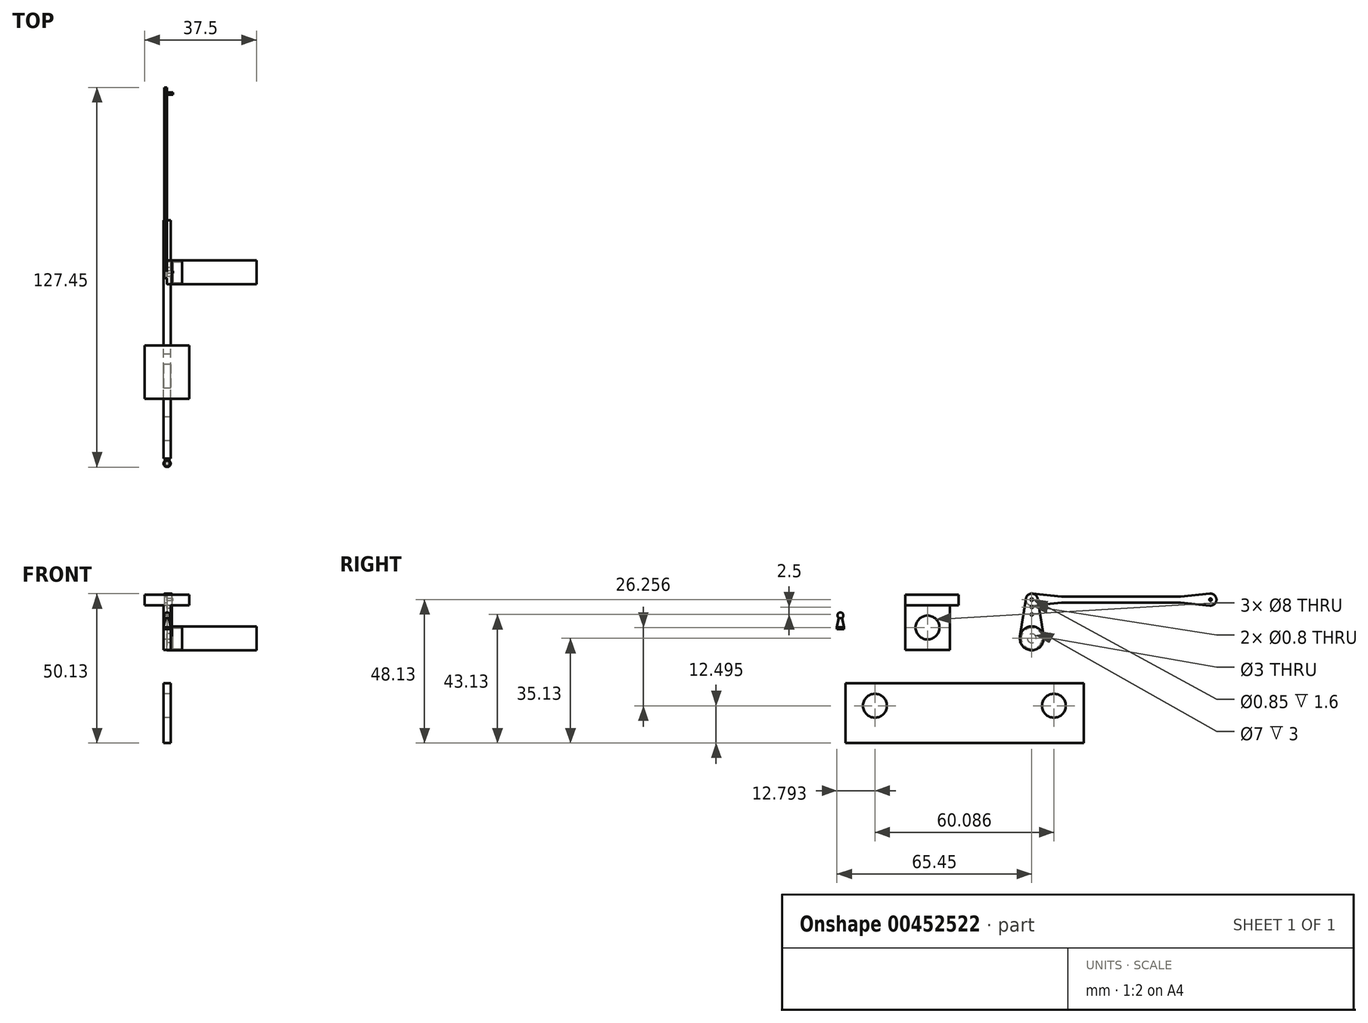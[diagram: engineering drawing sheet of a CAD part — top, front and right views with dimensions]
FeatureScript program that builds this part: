
annotation { "Feature Type Name" : "Feature", "Feature Type Description" : "" }
export const myFeature = defineFeature(function(context is Context, id is Id, definition is map)
    precondition{}
    {
        {
            var Q0;
            Q0=qCreatedBy(makeId("Right.planeOp"),FACE);
            var sketch = newSketch(context, id + "F0", { "sketchPlane" : qUnion([Q0])});
            skCircle(sketch, "E0", {"center": v(0, 0) * mm, "radius": 4 * mm});
            skCircle(sketch, "E1", {"center": v(0, 13) * mm, "radius": 2 * mm});
            skLineSegment(sketch, "E2", {"start": v(-1.98, 13.3) * mm, "end": v(-3.95, 0.62) * mm});
            skLineSegment(sketch, "E3", {"start": v(1.98, 13.3) * mm, "end": v(3.95, 0.62) * mm});
            skLineSegment(sketch, "E4", {"start": v(0, 13) * mm, "end": v(0, 0) * mm, "construction": true});
            skCircle(sketch, "E5", {"center": v(0, 0) * mm, "radius": 1.5 * mm});
            skCircle(sketch, "E6", {"center": v(0, 13) * mm, "radius": 0.42 * mm});
            skCircle(sketch, "E7.0.1.0", {"center": v(0, 10.5) * mm, "radius": 0.4 * mm});
            skLineSegment(sketch, "E7.direction2", {"start": v(0, 13) * mm, "end": v(0, 10.5) * mm, "construction": true});
            skCircle(sketch, "E8.0.1.0", {"center": v(0, 8) * mm, "radius": 0.4 * mm});
            skLineSegment(sketch, "E9", {"start": v(0, 10.5) * mm, "end": v(0, 8) * mm, "construction": true});
            skLineSegment(sketch, "E10", {"start": v(-17.13, 13) * mm, "end": v(24.81, 13) * mm, "construction": true});
            skLineSegment(sketch, "E11", {"start": v(-6.17, 15) * mm, "end": v(18.5, 15) * mm, "construction": true});
            skLineSegment(sketch, "E12", {"start": v(-6.02, 11) * mm, "end": v(18.13, 11) * mm, "construction": true});
            skLineSegment(sketch, "E13", {"start": v(14.47, 16) * mm, "end": v(14.47, 9.33) * mm, "construction": true});
            skCircle(sketch, "E14", {"center": v(9.9, 13) * mm, "radius": 1 * mm});
            skLineSegment(sketch, "E15", {"start": v(0.2, 14.99) * mm, "end": v(10, 14) * mm});
            skLineSegment(sketch, "E16", {"start": v(10, 12) * mm, "end": v(0, 10.99) * mm});
            skCircle(sketch, "E17", {"center": v(0, 13) * mm, "radius": 0.4 * mm});
            skLineSegment(sketch, "E18", {"start": v(10, 14) * mm, "end": v(30, 14) * mm});
            skLineSegment(sketch, "E19.MirrorCS", {"start": v(10, 12) * mm, "end": v(30, 12) * mm});
            skLineSegment(sketch, "E20", {"start": v(30, 14) * mm, "end": v(30, 12) * mm});
            skCircle(sketch, "E21", {"center": v(-35, 3.62) * mm, "radius": 4 * mm});
            skLineSegment(sketch, "E22", {"start": v(-45.57, 1.96) * mm, "end": v(-23.6, 1.96) * mm, "construction": true});
            skLineSegment(sketch, "E23", {"start": v(-35, 12.95) * mm, "end": v(-35, -6.89) * mm, "construction": true});
            skLineSegment(sketch, "E24.bottom", {"start": v(-42.5, 11.12) * mm, "end": v(-27.5, 11.12) * mm});
            skLineSegment(sketch, "E24.top", {"start": v(-42.5, -3.88) * mm, "end": v(-27.5, -3.88) * mm});
            skLineSegment(sketch, "E24.left", {"start": v(-42.5, 11.12) * mm, "end": v(-42.5, -3.88) * mm});
            skLineSegment(sketch, "E24.right", {"start": v(-27.5, 11.12) * mm, "end": v(-27.5, -3.88) * mm});
            skLineSegment(sketch, "E25.bottom", {"start": v(-42.5, 11.12) * mm, "end": v(-24.56, 11.12) * mm});
            skLineSegment(sketch, "E25.top", {"start": v(-42.5, 14.64) * mm, "end": v(-24.56, 14.64) * mm});
            skLineSegment(sketch, "E25.left", {"start": v(-42.5, 11.12) * mm, "end": v(-42.5, 14.64) * mm});
            skLineSegment(sketch, "E25.right", {"start": v(-24.56, 11.12) * mm, "end": v(-24.56, 14.64) * mm});
            skLineSegment(sketch, "E26", {"start": v(10, 14) * mm, "end": v(10, 23.15) * mm, "construction": true});
            skLineSegment(sketch, "E27", {"start": v(0, 13) * mm, "end": v(0, 25.95) * mm, "construction": true});
            skLineSegment(sketch, "E28", {"start": v(0, 22.2) * mm, "end": v(10, 22.2) * mm, "construction": true});
            skLineSegment(sketch, "E29.bottom", {"start": v(-62.57, -15.13) * mm, "end": v(17.43, -15.13) * mm});
            skLineSegment(sketch, "E29.top", {"start": v(-62.57, -35.13) * mm, "end": v(17.43, -35.13) * mm});
            skLineSegment(sketch, "E29.left", {"start": v(-62.57, -15.13) * mm, "end": v(-62.57, -35.13) * mm});
            skLineSegment(sketch, "E29.right", {"start": v(17.43, -15.13) * mm, "end": v(17.43, -35.13) * mm});
            skLineSegment(sketch, "E30.0", {"start": v(30.61, -22.63) * mm, "end": v(-81.37, -22.63) * mm, "construction": true});
            skPoint(sketch, "E31.endSnap0", {"position": v(17.43, -25.13) * mm});
            skLineSegment(sketch, "E32.0", {"start": v(-52.66, -4.93) * mm, "end": v(-52.66, -43.48) * mm, "construction": true});
            skLineSegment(sketch, "E33.0", {"start": v(7.43, -6.2) * mm, "end": v(7.43, -43.48) * mm, "construction": true});
            skCircle(sketch, "E34", {"center": v(-52.66, -22.63) * mm, "radius": 4 * mm});
            skCircle(sketch, "E35", {"center": v(7.43, -22.63) * mm, "radius": 4 * mm});
            skLineSegment(sketch, "E36", {"start": v(-64.25, 10) * mm, "end": v(-64.25, -2.92) * mm, "construction": true});
            skLineSegment(sketch, "E37", {"start": v(-68.41, 7.67) * mm, "end": v(-59.37, 7.67) * mm, "construction": true});
            skCircle(sketch, "E38", {"center": v(-64.25, 7.67) * mm, "radius": 1 * mm});
            skLineSegment(sketch, "E39", {"start": v(-67.7, 7.67) * mm, "end": v(-67.7, 3.67) * mm, "construction": true});
            skLineSegment(sketch, "E40.bottom", {"start": v(-64.77, 6.82) * mm, "end": v(-63.72, 6.82) * mm, "construction": true});
            skLineSegment(sketch, "E40.left", {"start": v(-64.77, 6.82) * mm, "end": v(-64.77, 3.18) * mm, "construction": true});
            skLineSegment(sketch, "E40.right", {"start": v(-63.72, 6.82) * mm, "end": v(-63.72, 3.18) * mm, "construction": true});
            skPoint(sketch, "E40.middle", {"position": v(-64.25, 5) * mm});
            skLineSegment(sketch, "E41", {"start": v(-67.7, 3.67) * mm, "end": v(-61.56, 3.67) * mm, "construction": true});
            skLineSegment(sketch, "E42", {"start": v(-64.77, 6.82) * mm, "end": v(-65.45, 3.67) * mm});
            skLineSegment(sketch, "E43", {"start": v(-65.45, 3.67) * mm, "end": v(-65.45, 3.14) * mm});
            skLineSegment(sketch, "E44", {"start": v(-65.45, 3.14) * mm, "end": v(-64.25, 3.14) * mm});
            skLineSegment(sketch, "E45.MirrorCS", {"start": v(-63.72, 6.82) * mm, "end": v(-63.05, 3.67) * mm});
            skLineSegment(sketch, "E46.MirrorCS", {"start": v(-63.05, 3.67) * mm, "end": v(-63.05, 3.14) * mm});
            skLineSegment(sketch, "E47.MirrorCS", {"start": v(-63.05, 3.14) * mm, "end": v(-64.25, 3.14) * mm});
            skLineSegment(sketch, "E48", {"start": v(-64.25, 8.67) * mm, "end": v(-64.25, 3.14) * mm});
            skCircle(sketch, "E49", {"center": v(50.94, 0) * mm, "radius": 4 * mm});
            skCircle(sketch, "E50", {"center": v(50.94, 13) * mm, "radius": 2 * mm});
            skLineSegment(sketch, "E51", {"start": v(48.96, 13.3) * mm, "end": v(46.99, 0.62) * mm});
            skLineSegment(sketch, "E52", {"start": v(52.92, 13.3) * mm, "end": v(54.9, 0.62) * mm});
            skLineSegment(sketch, "E53", {"start": v(50.94, 13) * mm, "end": v(50.94, 0) * mm, "construction": true});
            skCircle(sketch, "E54", {"center": v(50.94, 0) * mm, "radius": 1.5 * mm});
            skCircle(sketch, "E55", {"center": v(50.94, 13) * mm, "radius": 0.42 * mm});
            skCircle(sketch, "E56.0.1.0", {"center": v(50.94, 10.5) * mm, "radius": 0.4 * mm});
            skLineSegment(sketch, "E56.direction2", {"start": v(50.94, 13) * mm, "end": v(50.94, 10.5) * mm, "construction": true});
            skCircle(sketch, "E57.0.1.0", {"center": v(50.94, 8) * mm, "radius": 0.4 * mm});
            skLineSegment(sketch, "E58", {"start": v(50.94, 10.5) * mm, "end": v(50.94, 8) * mm, "construction": true});
            skCircle(sketch, "E59", {"center": v(50.94, 13) * mm, "radius": 0.4 * mm});
            skSolve(sketch);
        }
        {
            var Q0;
            {var subQ0=sQuery(id+"F0.wireOp",EDGE,"E2");Q0=makeQuery(id+"F0.imprint","IMPRINT",FACE,{"disambiguationData":[TD([[makeQuery(id+"F0.imprint","IMPRINT",EDGE,{"derivedFrom":subQ0}),1.0]])]});}
            var Q1;
            {var subQ0=sQuery(id+"F0.wireOp",EDGE,"E1");var subQ1=makeQuery(id+"F0.imprint","INTERSECT",VERTEX,{"derivedFrom":[subQ0,sQuery(id+"F0.wireOp",EDGE,"E2")]});Q1=makeQuery(id+"F0.imprint","IMPRINT",FACE,{"disambiguationData":[TD([[makeQuery(id+"F0.imprint","IMPRINT",EDGE,{"disambiguationData":[TD([[subQ1,1.0]])],"derivedFrom":subQ0}),1.0]])]});}
            var Q2;
            {var subQ0=sQuery(id+"F0.wireOp",EDGE,"E3");var subQ1=sQuery(id+"F0.wireOp",EDGE,"E1");var subQ2=makeQuery(id+"F0.imprint","INTERSECT",VERTEX,{"derivedFrom":[subQ1,subQ0]});Q2=makeQuery(id+"F0.imprint","IMPRINT",FACE,{"disambiguationData":[TD([[makeQuery(id+"F0.imprint","IMPRINT",EDGE,{"disambiguationData":[TD([[subQ2,1.0]])],"derivedFrom":subQ1}),-1.0]])]});}
            extrude(context, id + "F1", {"entities" : qUnion([Q0, Q1, Q2]), "depth" : 1.6 * mm});
        }
        {
            var Q0;
            Q0=makeQuery(id+"F0.imprint","IMPRINT",FACE,{"disambiguationData":[TD([[makeQuery(id+"F0.imprint","IMPRINT",EDGE,{"derivedFrom":sQuery(id+"F0.wireOp",EDGE,"E5")}),-1.0]])]});
            extrude(context, id + "F2", {"entities" : qUnion([Q0]), "operationType" : NewBodyOperationType.ADD, "depth" : 5 * mm});
        }
        {
            var Q0;
            Q0=makeQuery(id+"F2.opExtrude","CAP_FACE",FACE,{"disambiguationData":[OSD([sQuery(id+"F0.wireOp",EDGE,"E0"),sQuery(id+"F0.wireOp",EDGE,"E5")])],"isStart":false});
            var sketch = newSketch(context, id + "F3", { "sketchPlane" : qUnion([Q0])});
            skCircle(sketch, "E60", {"center": v(0, 0) * mm, "radius": 3.5 * mm});
            skSolve(sketch);
        }
        {
            var Q0;
            Q0=makeQuery(id+"F3.imprint","IMPRINT",FACE,{"disambiguationData":[TD([[makeQuery(id+"F3.imprint","IMPRINT",EDGE,{"derivedFrom":sQuery(id+"F3.wireOp",EDGE,"E60")}),1.0]])]});
            extrude(context, id + "F4", {"entities" : qUnion([Q0]), "operationType" : NewBodyOperationType.REMOVE, "oppositeDirection" : true, "depth" : 3 * mm});
        }
        {
            var Q0;
            {var subQ0=sQuery(id+"F0.wireOp",EDGE,"E15");Q0=makeQuery(id+"F0.imprint","IMPRINT",FACE,{"disambiguationData":[TD([[makeQuery(id+"F0.imprint","IMPRINT",EDGE,{"derivedFrom":subQ0}),-1.0]])]});}
            var Q1;
            Q1=makeQuery(id+"F0.imprint","IMPRINT",FACE,{"disambiguationData":[TD([[makeQuery(id+"F0.imprint","IMPRINT",EDGE,{"derivedFrom":sQuery(id+"F0.wireOp",EDGE,"E6")}),-1.0]])]});
            var Q2;
            {var subQ0=sQuery(id+"F0.wireOp",EDGE,"E3");var subQ1=sQuery(id+"F0.wireOp",EDGE,"E1");var subQ2=makeQuery(id+"F0.imprint","INTERSECT",VERTEX,{"derivedFrom":[subQ1,subQ0]});Q2=makeQuery(id+"F0.imprint","IMPRINT",FACE,{"disambiguationData":[TD([[makeQuery(id+"F0.imprint","IMPRINT",EDGE,{"disambiguationData":[TD([[subQ2,1.0]])],"derivedFrom":subQ1}),-1.0]])]});}
            var Q3;
            Q3=makeQuery(id+"F0.imprint","IMPRINT",FACE,{"disambiguationData":[TD([[makeQuery(id+"F0.imprint","IMPRINT",EDGE,{"derivedFrom":sQuery(id+"F0.wireOp",EDGE,"E17")}),1.0]])]});
            var Q4;
            Q4=makeQuery(id+"F0.imprint","IMPRINT",FACE,{"disambiguationData":[TD([[makeQuery(id+"F0.imprint","IMPRINT",EDGE,{"derivedFrom":sQuery(id+"F0.wireOp",EDGE,"E6")}),1.0]])]});
            var Q5;
            {var subQ0=sQuery(id+"F0.wireOp",EDGE,"E18");Q5=makeQuery(id+"F0.imprint","IMPRINT",FACE,{"disambiguationData":[TD([[makeQuery(id+"F0.imprint","IMPRINT",EDGE,{"derivedFrom":subQ0}),-1.0]])]});}
            var Q6;
            {var subQ0=sQuery(id+"F0.wireOp",EDGE,"E14");var subQ1=makeQuery(id+"F0.imprint","INTERSECT",VERTEX,{"derivedFrom":[subQ0,sQuery(id+"F0.wireOp",EDGE,"E15"),sQuery(id+"F0.wireOp",EDGE,"E18")]});Q6=makeQuery(id+"F0.imprint","IMPRINT",FACE,{"disambiguationData":[TD([[makeQuery(id+"F0.imprint","IMPRINT",EDGE,{"disambiguationData":[TD([[subQ1,-1.0]])],"derivedFrom":subQ0}),1.0]])]});}
            extrude(context, id + "F5", {"entities" : qUnion([Q0, Q1, Q2, Q3, Q4, Q5, Q6]), "oppositeDirection" : true, "depth" : 1 * mm});
        }
        {
            var Q0;
            Q0=makeQuery(id+"F0.imprint","IMPRINT",FACE,{"disambiguationData":[TD([[makeQuery(id+"F0.imprint","IMPRINT",EDGE,{"derivedFrom":sQuery(id+"F0.wireOp",EDGE,"E17")}),1.0]])]});
            extrude(context, id + "F6", {"entities" : qUnion([Q0]), "operationType" : NewBodyOperationType.ADD, "depth" : 2 * mm});
        }
        {
            var Q0;
            Q0=makeQuery(id+"F5.opExtrude","SWEPT_BODY",BODY,{"disambiguationData":[OSD([sQuery(id+"F0.wireOp",EDGE,"E1"),sQuery(id+"F0.wireOp",EDGE,"E15"),sQuery(id+"F0.wireOp",EDGE,"E16"),sQuery(id+"F0.wireOp",EDGE,"E18"),sQuery(id+"F0.wireOp",EDGE,"E19.MirrorCS"),sQuery(id+"F0.wireOp",EDGE,"E20")])]});
            var Q1;
            Q1=makeQuery(id+"F5.opExtrude","SWEPT_FACE",FACE,{"disambiguationData":[OSD([sQuery(id+"F0.wireOp",EDGE,"E20")])]});
            mirror(context, id + "F7", {"operationType" : NewBodyOperationType.ADD, "entities" : qUnion([Q0]), "mirrorPlane" : qUnion([Q1])});
        }
        {
            var Q0;
            Q0=makeQuery(id+"F0.imprint","IMPRINT",FACE,{"disambiguationData":[TD([[makeQuery(id+"F0.imprint","IMPRINT",EDGE,{"derivedFrom":sQuery(id+"F0.wireOp",EDGE,"E5")}),-1.0]])]});
            var Q1;
            Q1=makeQuery(id+"F0.imprint","IMPRINT",FACE,{"disambiguationData":[TD([[makeQuery(id+"F0.imprint","IMPRINT",EDGE,{"derivedFrom":sQuery(id+"F0.wireOp",EDGE,"E5")}),1.0]])]});
            extrude(context, id + "F8", {"entities" : qUnion([Q0, Q1]), "depth" : 30 * mm});
        }
        {
            var Q0;
            Q0=makeQuery(id+"F1.opExtrude","SWEPT_BODY",BODY,{"disambiguationData":[OSD([sQuery(id+"F0.wireOp",EDGE,"E0"),sQuery(id+"F0.wireOp",EDGE,"E1"),sQuery(id+"F0.wireOp",EDGE,"E2"),sQuery(id+"F0.wireOp",EDGE,"E3"),sQuery(id+"F0.wireOp",EDGE,"E6"),sQuery(id+"F0.wireOp",EDGE,"E7.0.1.0"),sQuery(id+"F0.wireOp",EDGE,"E8.0.1.0")])]});
            var Q1;
            Q1=makeQuery(id+"F8.opExtrude","SWEPT_BODY",BODY,{"disambiguationData":[OSD([sQuery(id+"F0.wireOp",EDGE,"E0")])]});
            booleanBodies(context, id + "F9", {"operationType" : BooleanOperationType.SUBTRACTION, "tools" : qUnion([Q0]), "targets" : qUnion([Q1]), "keepTools" : true});
        }
        {
            var Q0;
            Q0=makeQuery(id+"F0.imprint","IMPRINT",FACE,{"disambiguationData":[TD([[makeQuery(id+"F0.imprint","IMPRINT",EDGE,{"derivedFrom":sQuery(id+"F0.wireOp",EDGE,"E21")}),-1.0]])]});
            extrude(context, id + "F10", {"entities" : qUnion([Q0]), "depth" : 2.5 * mm, "symmetric" : true});
        }
        {
            var Q0;
            Q0=makeQuery(id+"F0.imprint","IMPRINT",FACE,{"disambiguationData":[TD([[makeQuery(id+"F0.imprint","IMPRINT",EDGE,{"derivedFrom":sQuery(id+"F0.wireOp",EDGE,"E25.top")}),-1.0]])]});
            extrude(context, id + "F11", {"entities" : qUnion([Q0]), "operationType" : NewBodyOperationType.ADD, "depth" : 15 * mm, "symmetric" : true});
        }
        {
            var Q0;
            Q0=makeQuery(id+"F0.imprint","IMPRINT",FACE,{"disambiguationData":[TD([[makeQuery(id+"F0.imprint","IMPRINT",EDGE,{"derivedFrom":sQuery(id+"F0.wireOp",EDGE,"E29.bottom")}),-1.0]])]});
            extrude(context, id + "F12", {"entities" : qUnion([Q0]), "depth" : 2.5 * mm, "symmetric" : true});
        }
        {
            var Q0;
            {var subQ0=sQuery(id+"F0.wireOp",EDGE,"E38");var subQ1=makeQuery(id+"F0.imprint","INTERSECT",VERTEX,{"derivedFrom":[subQ0,sQuery(id+"F0.wireOp",EDGE,"E42")]});Q0=makeQuery(id+"F0.imprint","IMPRINT",FACE,{"disambiguationData":[TD([[makeQuery(id+"F0.imprint","IMPRINT",EDGE,{"disambiguationData":[TD([[subQ1,1.0]])],"derivedFrom":subQ0}),1.0]])]});}
            var Q1;
            {var subQ0=sQuery(id+"F0.wireOp",EDGE,"E42");Q1=makeQuery(id+"F0.imprint","IMPRINT",FACE,{"disambiguationData":[TD([[makeQuery(id+"F0.imprint","IMPRINT",EDGE,{"derivedFrom":subQ0}),1.0]])]});}
            var Q2;
            Q2=sQuery(id+"F0.wireOp",EDGE,"E36");
            revolve(context, id + "F13", {"entities" : qUnion([Q0, Q1]), "axis" : qUnion([Q2]), "revolveType" : RevolveType.FULL});
        }
    });
